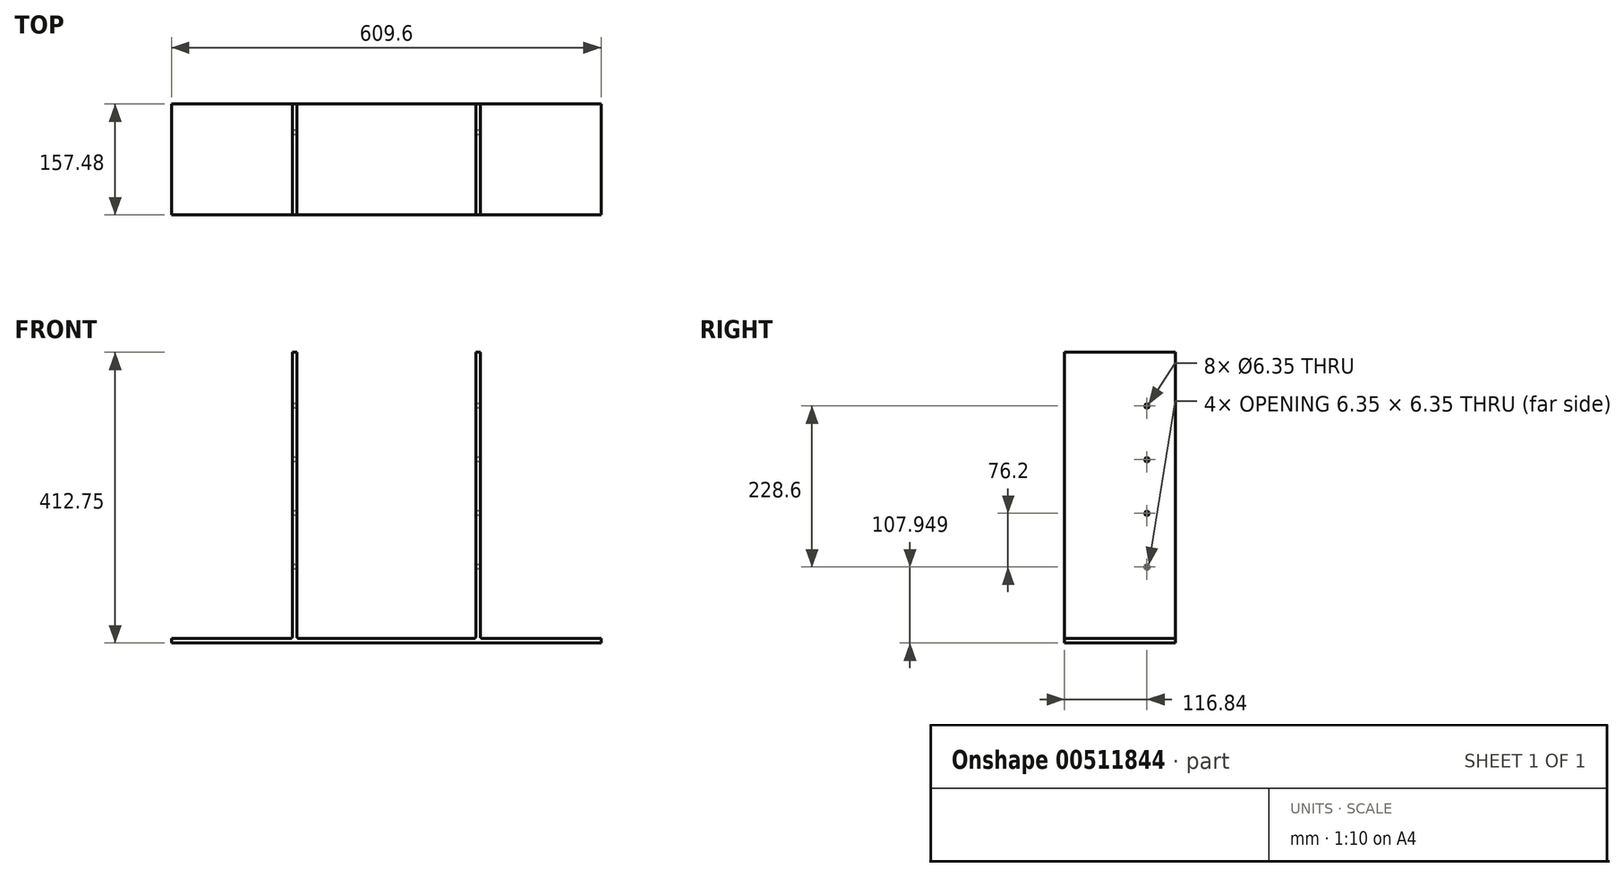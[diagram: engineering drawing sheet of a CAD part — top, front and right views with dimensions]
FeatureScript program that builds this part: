
annotation { "Feature Type Name" : "Feature", "Feature Type Description" : "" }
export const myFeature = defineFeature(function(context is Context, id is Id, definition is map)
    precondition{}
    {
        {
            var Q0;
            Q0=qCreatedBy(makeId("Front.planeOp"),FACE);
            var sketch = newSketch(context, id + "F0", { "sketchPlane" : qUnion([Q0])});
            skLineSegment(sketch, "E0", {"start": v(-103.56, -63.28) * mm, "end": v(201.24, -63.28) * mm});
            skLineSegment(sketch, "E1", {"start": v(201.24, -63.28) * mm, "end": v(201.24, -56.93) * mm});
            skLineSegment(sketch, "E2", {"start": v(201.24, -56.93) * mm, "end": v(32.96, -56.93) * mm});
            skLineSegment(sketch, "E3", {"start": v(29.79, -53.76) * mm, "end": v(29.79, 349.47) * mm});
            skLineSegment(sketch, "E4", {"start": v(29.79, 349.47) * mm, "end": v(23.44, 349.47) * mm});
            skLineSegment(sketch, "E5", {"start": v(23.44, 349.47) * mm, "end": v(23.44, -53.76) * mm});
            skLineSegment(sketch, "E6", {"start": v(-103.56, -63.28) * mm, "end": v(-103.56, -56.93) * mm});
            skLineSegment(sketch, "E7", {"start": v(20.26, -56.93) * mm, "end": v(-103.56, -56.93) * mm});
            skLineSegment(sketch, "E8.MirrorCS", {"start": v(-408.36, -63.28) * mm, "end": v(-408.36, -56.93) * mm});
            skLineSegment(sketch, "E9.MirrorCS", {"start": v(-236.91, 349.47) * mm, "end": v(-230.56, 349.47) * mm});
            skLineSegment(sketch, "E10.MirrorCS", {"start": v(-230.56, 349.47) * mm, "end": v(-230.56, -53.76) * mm});
            skLineSegment(sketch, "E11.MirrorCS", {"start": v(-408.36, -56.93) * mm, "end": v(-240.09, -56.93) * mm});
            skLineSegment(sketch, "E12.MirrorCS", {"start": v(-236.91, -53.76) * mm, "end": v(-236.91, 349.47) * mm});
            skLineSegment(sketch, "E13.MirrorCS", {"start": v(-227.39, -56.93) * mm, "end": v(-103.56, -56.93) * mm});
            skLineSegment(sketch, "E14.MirrorCS", {"start": v(-103.56, -63.28) * mm, "end": v(-408.36, -63.28) * mm});
            skPoint(sketch, "E15.visualSharp", {"position": v(-236.91, -56.93) * mm});
            skArc(sketch, "E15.filletArc", {"start": v(-240.09, -56.93) * mm, "mid": v(-237.84, -56) * mm, "end": v(-236.91, -53.76) * mm});
            skPoint(sketch, "E16.visualSharp", {"position": v(-230.56, -56.93) * mm});
            skArc(sketch, "E16.filletArc", {"start": v(-230.56, -53.76) * mm, "mid": v(-229.63, -56) * mm, "end": v(-227.39, -56.93) * mm});
            skPoint(sketch, "E17.visualSharp", {"position": v(23.44, -56.93) * mm});
            skArc(sketch, "E17.filletArc", {"start": v(20.26, -56.93) * mm, "mid": v(22.5, -56) * mm, "end": v(23.44, -53.76) * mm});
            skPoint(sketch, "E18.visualSharp", {"position": v(29.79, -56.93) * mm});
            skArc(sketch, "E18.filletArc", {"start": v(29.79, -53.76) * mm, "mid": v(30.72, -56) * mm, "end": v(32.96, -56.93) * mm});
            skSolve(sketch);
        }
        {
            var Q0;
            Q0=makeQuery(id+"F0.imprint","IMPRINT",FACE,{"disambiguationData":[TD([[makeQuery(id+"F0.imprint","IMPRINT",EDGE,{"derivedFrom":sQuery(id+"F0.wireOp",EDGE,"E0")}),1.0]])]});
            var Q1;
            Q1=makeQuery(id+"F0.imprint","IMPRINT",FACE,{"disambiguationData":[TD([[makeQuery(id+"F0.imprint","IMPRINT",EDGE,{"derivedFrom":sQuery(id+"F0.wireOp",EDGE,"E6")}),1.0]])]});
            extrude(context, id + "F1", {"entities" : qUnion([Q0, Q1]), "depth" : 157.48 * mm, "offsetDistance" : 25.4 * mm});
        }
        {
            var Q0;
            Q0=makeQuery(id+"F1.opExtrude","SWEPT_FACE",FACE,{"disambiguationData":[OSD([sQuery(id+"F0.wireOp",EDGE,"E12.MirrorCS")])]});
            var sketch = newSketch(context, id + "F2", { "sketchPlane" : qUnion([Q0])});
            skLineSegment(sketch, "E19", {"start": v(78.74, 349.47) * mm, "end": v(78.74, -53.76) * mm, "construction": true});
            skLineSegment(sketch, "E20.0", {"start": v(40.64, 349.47) * mm, "end": v(40.64, -53.76) * mm, "construction": true});
            skLineSegment(sketch, "E21.MirrorCS", {"start": v(116.84, 349.47) * mm, "end": v(116.84, -53.76) * mm, "construction": true});
            skCircle(sketch, "E22", {"center": v(40.64, 273.27) * mm, "radius": 3.18 * mm});
            skCircle(sketch, "E23", {"center": v(40.64, 197.07) * mm, "radius": 3.18 * mm});
            skCircle(sketch, "E24", {"center": v(40.64, 120.87) * mm, "radius": 3.18 * mm});
            skCircle(sketch, "E25", {"center": v(40.64, 44.67) * mm, "radius": 3.18 * mm});
            skCircle(sketch, "E26.MirrorC", {"center": v(116.84, 273.27) * mm, "radius": 3.18 * mm});
            skCircle(sketch, "E27.MirrorC", {"center": v(116.84, 197.07) * mm, "radius": 3.18 * mm});
            skCircle(sketch, "E28.MirrorC", {"center": v(116.84, 120.87) * mm, "radius": 3.18 * mm});
            skCircle(sketch, "E29.MirrorC", {"center": v(116.84, 44.67) * mm, "radius": 3.18 * mm});
            skSolve(sketch);
        }
        {
            var Q0;
            Q0=makeQuery(id+"F2.imprint","IMPRINT",FACE,{"disambiguationData":[TD([[makeQuery(id+"F2.imprint","IMPRINT",EDGE,{"derivedFrom":sQuery(id+"F2.wireOp",EDGE,"E22")}),1.0]])]});
            var Q1;
            Q1=makeQuery(id+"F2.imprint","IMPRINT",FACE,{"disambiguationData":[TD([[makeQuery(id+"F2.imprint","IMPRINT",EDGE,{"derivedFrom":sQuery(id+"F2.wireOp",EDGE,"E23")}),1.0]])]});
            var Q2;
            Q2=makeQuery(id+"F2.imprint","IMPRINT",FACE,{"disambiguationData":[TD([[makeQuery(id+"F2.imprint","IMPRINT",EDGE,{"derivedFrom":sQuery(id+"F2.wireOp",EDGE,"E24")}),1.0]])]});
            var Q3;
            Q3=makeQuery(id+"F2.imprint","IMPRINT",FACE,{"disambiguationData":[TD([[makeQuery(id+"F2.imprint","IMPRINT",EDGE,{"derivedFrom":sQuery(id+"F2.wireOp",EDGE,"E25")}),1.0]])]});
            var Q4;
            Q4=makeQuery(id+"F2.imprint","IMPRINT",FACE,{"disambiguationData":[TD([[makeQuery(id+"F2.imprint","IMPRINT",EDGE,{"derivedFrom":sQuery(id+"F2.wireOp",EDGE,"E29.MirrorC")}),-1.0]])]});
            var Q5;
            Q5=makeQuery(id+"F2.imprint","IMPRINT",FACE,{"disambiguationData":[TD([[makeQuery(id+"F2.imprint","IMPRINT",EDGE,{"derivedFrom":sQuery(id+"F2.wireOp",EDGE,"E28.MirrorC")}),-1.0]])]});
            var Q6;
            Q6=makeQuery(id+"F2.imprint","IMPRINT",FACE,{"disambiguationData":[TD([[makeQuery(id+"F2.imprint","IMPRINT",EDGE,{"derivedFrom":sQuery(id+"F2.wireOp",EDGE,"E27.MirrorC")}),-1.0]])]});
            var Q7;
            Q7=makeQuery(id+"F2.imprint","IMPRINT",FACE,{"disambiguationData":[TD([[makeQuery(id+"F2.imprint","IMPRINT",EDGE,{"derivedFrom":sQuery(id+"F2.wireOp",EDGE,"E26.MirrorC")}),-1.0]])]});
            extrude(context, id + "F3", {"entities" : qUnion([Q0, Q1, Q2, Q3, Q4, Q5, Q6, Q7]), "operationType" : NewBodyOperationType.REMOVE, "endBound" : BoundingType.THROUGH_ALL, "oppositeDirection" : true, "depth" : 25.4 * mm, "offsetDistance" : 25.4 * mm});
        }
    });
